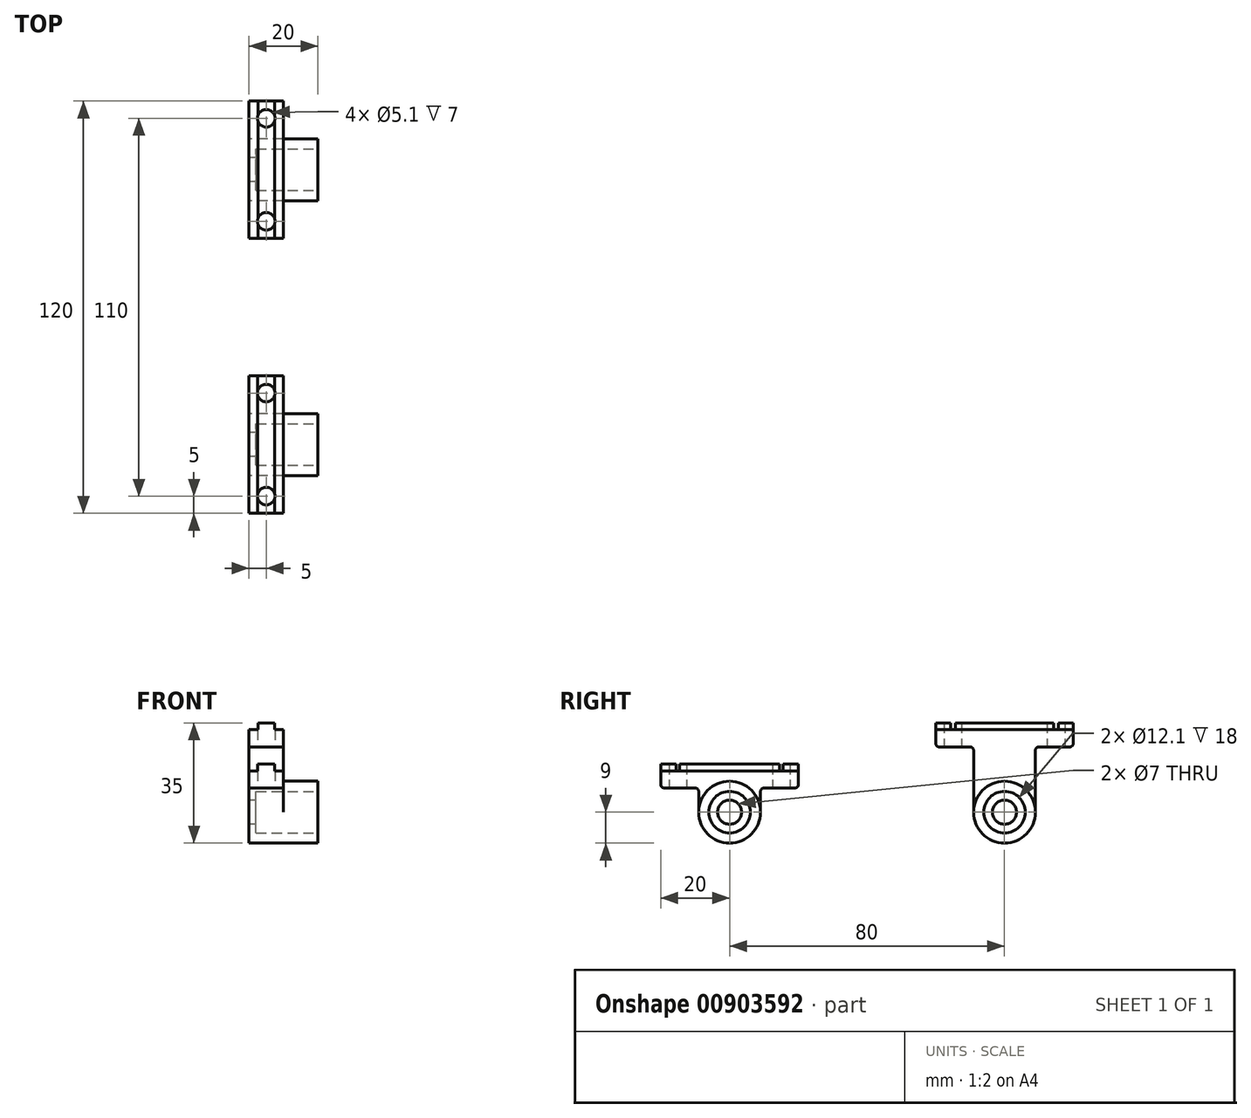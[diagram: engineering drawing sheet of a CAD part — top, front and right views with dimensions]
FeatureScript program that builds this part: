
annotation { "Feature Type Name" : "Feature", "Feature Type Description" : "" }
export const myFeature = defineFeature(function(context is Context, id is Id, definition is map)
    precondition{}
    {
        {
            var Q0;
            Q0=qCreatedBy(makeId("Right.planeOp"),FACE);
            var sketch = newSketch(context, id + "F0", { "sketchPlane" : qUnion([Q0])});
            skCircle(sketch, "E0", {"center": v(0, 0) * mm, "radius": 9 * mm});
            skSolve(sketch);
        }
        {
            var Q0;
            Q0=qSketchRegion(id+"F0",true);
            extrude(context, id + "F1", {"entities" : qUnion([Q0]), "depth" : 20 * mm, "offsetDistance" : 25 * mm});
        }
        {
            var Q0;
            Q0=qCreatedBy(makeId("Front.planeOp"),FACE);
            cPlane(context, id + "F2", {"entities" : qUnion([Q0]), "cplaneType" : CPlaneType.OFFSET, "offset" : 40 * mm, "oppositeDirection" : true, "width" : 150 * mm, "height" : 150 * mm});
        }
        {
            var Q0;
            Q0=qCreatedBy(makeId("Front.planeOp"),FACE);
            var sketch = newSketch(context, id + "F3", { "sketchPlane" : qUnion([Q0])});
            skLineSegment(sketch, "E1.bottom", {"start": v(0, 24) * mm, "end": v(2.55, 24) * mm});
            skLineSegment(sketch, "E1.top", {"start": v(0, 0) * mm, "end": v(10, 0) * mm});
            skLineSegment(sketch, "E1.left", {"start": v(0, 24) * mm, "end": v(0, 0) * mm});
            skLineSegment(sketch, "E1.right", {"start": v(10, 24) * mm, "end": v(10, 0) * mm});
            skLineSegment(sketch, "E2.bottom", {"start": v(2.55, 26) * mm, "end": v(7.45, 26) * mm});
            skLineSegment(sketch, "E2.left", {"start": v(2.55, 26) * mm, "end": v(2.55, 24) * mm});
            skLineSegment(sketch, "E2.right", {"start": v(7.45, 26) * mm, "end": v(7.45, 24) * mm});
            skPoint(sketch, "E2.middle", {"position": v(5, 24) * mm});
            skLineSegment(sketch, "E3.trimOffspring", {"start": v(7.45, 24) * mm, "end": v(10, 24) * mm});
            skSolve(sketch);
        }
        {
            var Q0;
            Q0=qSketchRegion(id+"F3",true);
            extrude(context, id + "F4", {"entities" : qUnion([Q0]), "operationType" : NewBodyOperationType.ADD, "endBound" : BoundingType.SYMMETRIC, "depth" : 40 * mm});
        }
        {
            var Q0;
            Q0=makeQuery(id+"F1.opExtrude","SWEPT_BODY",BODY,{"disambiguationData":[OSD([sQuery(id+"F0.wireOp",EDGE,"E0")])]});
            var Q1;
            Q1=qCreatedBy(id+"F2.planeOp",FACE);
            mirror(context, id + "F5", {"entities" : qUnion([Q0]), "mirrorPlane" : qUnion([Q1])});
        }
        {
            var Q0;
            Q0=makeQuery(id+"F4.opExtrude","CAP_FACE",FACE,{"disambiguationData":[OSD([sQuery(id+"F3.wireOp",EDGE,"E1.bottom"),sQuery(id+"F3.wireOp",EDGE,"E1.top"),sQuery(id+"F3.wireOp",EDGE,"E1.left"),sQuery(id+"F3.wireOp",EDGE,"E1.right"),sQuery(id+"F3.wireOp",EDGE,"E2.bottom"),sQuery(id+"F3.wireOp",EDGE,"E2.left"),sQuery(id+"F3.wireOp",EDGE,"E2.right"),sQuery(id+"F3.wireOp",EDGE,"E3.trimOffspring")])],"isStart":false});
            var sketch = newSketch(context, id + "F6", { "sketchPlane" : qUnion([Q0])});
            skLineSegment(sketch, "E4", {"start": v(0, 12) * mm, "end": v(2.5, 12) * mm});
            skLineSegment(sketch, "E5", {"start": v(2.5, 12) * mm, "end": v(2.5, 14) * mm});
            skLineSegment(sketch, "E6", {"start": v(2.5, 14) * mm, "end": v(7.5, 14) * mm});
            skLineSegment(sketch, "E7", {"start": v(7.5, 14) * mm, "end": v(7.5, 12) * mm});
            skLineSegment(sketch, "E8", {"start": v(7.5, 12) * mm, "end": v(10, 12) * mm});
            skLineSegment(sketch, "E9", {"start": v(0, 12) * mm, "end": v(0, 26) * mm});
            skLineSegment(sketch, "E10", {"start": v(0, 26) * mm, "end": v(10, 26) * mm});
            skLineSegment(sketch, "E11", {"start": v(10, 26) * mm, "end": v(10, 12) * mm});
            skSolve(sketch);
        }
        {
            var Q0;
            Q0=qSketchRegion(id+"F6",true);
            extrude(context, id + "F7", {"entities" : qUnion([Q0]), "operationType" : NewBodyOperationType.REMOVE, "oppositeDirection" : true, "depth" : 40 * mm});
        }
        {
            var Q0;
            Q0=makeQuery(id+"F4.opExtrude","SWEPT_FACE",FACE,{"disambiguationData":[OSD([sQuery(id+"F3.wireOp",EDGE,"E1.right")])]});
            var sketch = newSketch(context, id + "F8", { "sketchPlane" : qUnion([Q0])});
            skLineSegment(sketch, "E12", {"start": v(-19, 7) * mm, "end": v(-10, 7) * mm});
            skLineSegment(sketch, "E13", {"start": v(-9, 6) * mm, "end": v(-9, 0) * mm});
            skPoint(sketch, "E14.visualSharp", {"position": v(-9, 7) * mm});
            skArc(sketch, "E14.filletArc", {"start": v(-9, 6) * mm, "mid": v(-9.3, 6.7) * mm, "end": v(-10, 7) * mm});
            skLineSegment(sketch, "E15", {"start": v(0, 0) * mm, "end": v(0, 6.2) * mm, "construction": true});
            skLineSegment(sketch, "E16", {"start": v(-20, 0) * mm, "end": v(-20, 8) * mm});
            skPoint(sketch, "E17.visualSharp", {"position": v(-20, 7) * mm});
            skArc(sketch, "E17.filletArc", {"start": v(-20, 8) * mm, "mid": v(-19.7, 7.3) * mm, "end": v(-19, 7) * mm});
            skLineSegment(sketch, "E18.MirrorCS", {"start": v(9, 6) * mm, "end": v(9, 0) * mm});
            skArc(sketch, "E19.MirrorCS", {"start": v(9, 6) * mm, "mid": v(9.3, 6.7) * mm, "end": v(10, 7) * mm});
            skLineSegment(sketch, "E20.MirrorCS", {"start": v(19, 7) * mm, "end": v(10, 7) * mm});
            skArc(sketch, "E21.MirrorCS", {"start": v(20, 8) * mm, "mid": v(19.7, 7.3) * mm, "end": v(19, 7) * mm});
            skLineSegment(sketch, "E22.MirrorCS", {"start": v(20, 0) * mm, "end": v(20, 8) * mm});
            skLineSegment(sketch, "E23", {"start": v(-20, 0) * mm, "end": v(-9, 0) * mm});
            skLineSegment(sketch, "E24.MirrorCS", {"start": v(20, 0) * mm, "end": v(9, 0) * mm});
            skLineSegment(sketch, "E25", {"start": v(60, 20) * mm, "end": v(60, 0) * mm});
            skLineSegment(sketch, "E26", {"start": v(60, 0) * mm, "end": v(71, 0) * mm});
            skLineSegment(sketch, "E27", {"start": v(71, 0) * mm, "end": v(71, 18) * mm});
            skLineSegment(sketch, "E28", {"start": v(70, 19) * mm, "end": v(61, 19) * mm});
            skArc(sketch, "E29", {"start": v(60, 20) * mm, "mid": v(60.3, 19.3) * mm, "end": v(61, 19) * mm});
            skPoint(sketch, "E30.visualSharp", {"position": v(71, 19) * mm});
            skArc(sketch, "E30.filletArc", {"start": v(71, 18) * mm, "mid": v(70.7, 18.7) * mm, "end": v(70, 19) * mm});
            skLineSegment(sketch, "E31", {"start": v(100, 20) * mm, "end": v(100, 0) * mm});
            skLineSegment(sketch, "E32", {"start": v(100, 0) * mm, "end": v(89, 0) * mm});
            skLineSegment(sketch, "E33", {"start": v(89, 0) * mm, "end": v(89, 18) * mm});
            skLineSegment(sketch, "E34", {"start": v(90, 19) * mm, "end": v(99, 19) * mm});
            skArc(sketch, "E35", {"start": v(99, 19) * mm, "mid": v(99.7, 19.3) * mm, "end": v(100, 20) * mm});
            skPoint(sketch, "E36.visualSharp", {"position": v(89, 19) * mm});
            skArc(sketch, "E36.filletArc", {"start": v(90, 19) * mm, "mid": v(89.3, 18.7) * mm, "end": v(89, 18) * mm});
            skSolve(sketch);
        }
        {
            var Q0;
            Q0=qSketchRegion(id+"F8",true);
            extrude(context, id + "F9", {"entities" : qUnion([Q0]), "operationType" : NewBodyOperationType.REMOVE, "oppositeDirection" : true, "depth" : 25 * mm});
        }
        {
            var Q0;
            Q0=makeQuery(id+"F1.opExtrude","CAP_FACE",FACE,{"disambiguationData":[OSD([sQuery(id+"F0.wireOp",EDGE,"E0")])],"isStart":false});
            var sketch = newSketch(context, id + "F10", { "sketchPlane" : qUnion([Q0])});
            skCircle(sketch, "E37", {"center": v(0, 0) * mm, "radius": 6.05 * mm});
            skCircle(sketch, "E38", {"center": v(80, 0) * mm, "radius": 6.05 * mm});
            skSolve(sketch);
        }
        {
            var Q0;
            Q0=qSketchRegion(id+"F10",true);
            extrude(context, id + "F11", {"entities" : qUnion([Q0]), "operationType" : NewBodyOperationType.REMOVE, "oppositeDirection" : true, "depth" : 18 * mm});
        }
        {
            var Q0;
            Q0=makeQuery(id+"F1.opExtrude","CAP_FACE",FACE,{"disambiguationData":[OSD([sQuery(id+"F0.wireOp",EDGE,"E0")])],"isStart":true});
            var sketch = newSketch(context, id + "F12", { "sketchPlane" : qUnion([Q0])});
            skCircle(sketch, "E39", {"center": v(0, 0) * mm, "radius": 3.5 * mm});
            skCircle(sketch, "E40", {"center": v(-80, 0) * mm, "radius": 3.5 * mm});
            skSolve(sketch);
        }
        {
            var Q0;
            Q0=qSketchRegion(id+"F12",true);
            extrude(context, id + "F13", {"entities" : qUnion([Q0]), "operationType" : NewBodyOperationType.REMOVE, "oppositeDirection" : true, "depth" : 25 * mm});
        }
        {
            var Q0;
            Q0=makeQuery(id+"F9.boolean.opBoolean","COPY",FACE,{"derivedFrom":makeQuery(id+"F9.opExtrude","SWEPT_FACE",FACE,{"disambiguationData":[OSD([sQuery(id+"F8.wireOp",EDGE,"E12")])]})});
            var sketch = newSketch(context, id + "F14", { "sketchPlane" : qUnion([Q0])});
            skCircle(sketch, "E41", {"center": v(5, 15) * mm, "radius": 2.55 * mm});
            skPoint(sketch, "E41.centerSnap0", {"position": v(5, 19) * mm});
            skCircle(sketch, "E42", {"center": v(5, -15) * mm, "radius": 2.55 * mm});
            skLineSegment(sketch, "E43", {"start": v(-16.55, -40) * mm, "end": v(11.7, -40) * mm, "construction": true});
            skCircle(sketch, "E44.MirrorC", {"center": v(5, -65) * mm, "radius": 2.55 * mm});
            skCircle(sketch, "E45.MirrorC", {"center": v(5, -95) * mm, "radius": 2.55 * mm});
            skSolve(sketch);
        }
        {
            var Q0;
            Q0=qSketchRegion(id+"F14",true);
            extrude(context, id + "F15", {"entities" : qUnion([Q0]), "operationType" : NewBodyOperationType.REMOVE, "endBound" : BoundingType.THROUGH_ALL, "oppositeDirection" : true, "depth" : 25 * mm});
        }
    });
